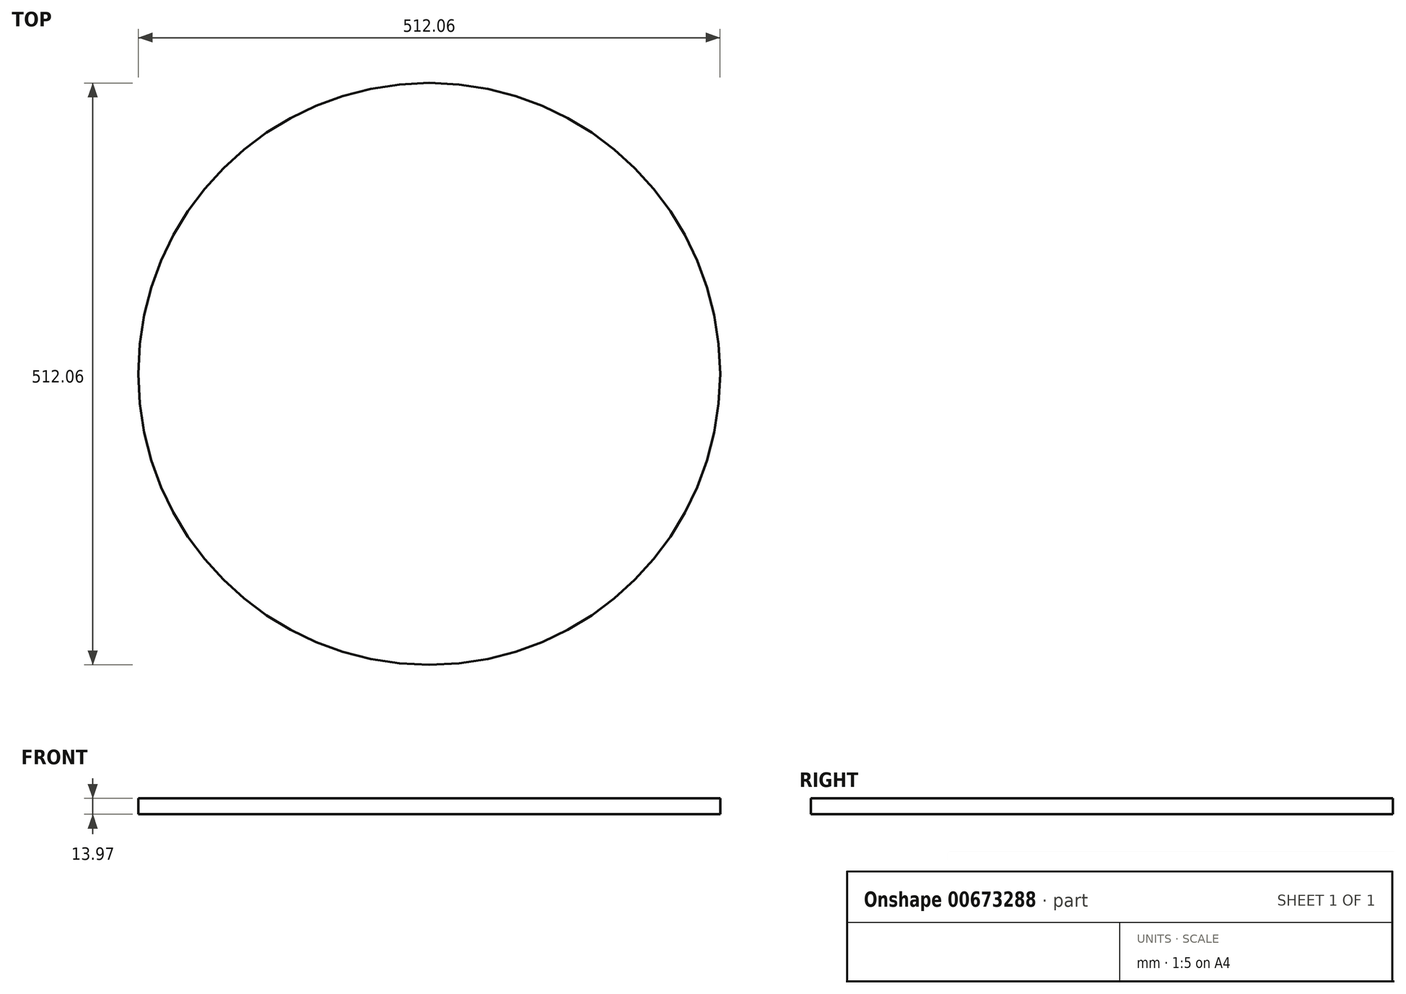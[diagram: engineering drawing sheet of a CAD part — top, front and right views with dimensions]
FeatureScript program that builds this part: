
annotation { "Feature Type Name" : "Feature", "Feature Type Description" : "" }
export const myFeature = defineFeature(function(context is Context, id is Id, definition is map)
    precondition{}
    {
        {
            var Q0;
            Q0=qCreatedBy(makeId("Top.planeOp"),FACE);
            var sketch = newSketch(context, id + "F0", { "sketchPlane" : qUnion([Q0])});
            skCircle(sketch, "E0", {"center": v(0, 0) * mm, "radius": 256.03 * mm});
            skSolve(sketch);
        }
        {
            var Q0;
            Q0=makeQuery(id+"F0.imprint","IMPRINT",FACE,{"disambiguationData":[TD([[makeQuery(id+"F0.imprint","IMPRINT",EDGE,{"derivedFrom":sQuery(id+"F0.wireOp",EDGE,"E0")}),1.0]])]});
            extrude(context, id + "F1", {"entities" : qUnion([Q0]), "depth" : 13.97 * mm, "offsetDistance" : 25.4 * mm});
        }
    });
